# Revit family: LeL Lira 1.0
name_source: partatom
category: Lighting Fixtures
units: mm (PartAtom-declared; Revit-internal decimal feet)

## family parameters
Cut with Voids When Loaded = Yes
Host = Face
Light Source = No
Part Type = Normal
Room Calculation Point = No
Round Connector Dimension = Use Diameter
Shared = No

## types (4) — shared parameters
Alimentazione = 230 V
Apparent Load = 6 VA
CCT = 3000 K
CRI = 80
Default Elevation = 1219 mm
Description = Outdoor Wall Mounted
IK = IK08
IP = IP65
Lamp = LED
Manufacturer = L&L Luce&Light
Model = LR10
Rated Power supply = 230 V
URL = https://www.lucelight.it
Wattage = 6 W
Weight = 0.53 kg

## per-type parameters (varying)
| type | Finish | Lumen Output | Photometry |
| 1.0 A 6W 230Vac white | LeL White | 368 lm | LR10 Light source : 1.0 A white |
| 1.0 A 6W 230Vac cor-ten | LeL Cor-ten | 278 lm | LR10 Light source : 1.0 A corten |
| 1.0 A 6W 230Vac anthracite | LeL Anthracite | 278 lm | LR10 Light source : 1.0 A antracite |
| 1.0 A 6W 230Vac grey | LeL Grey | 368 lm | LR10 Light source : 1.0 A grey |

## geometry (parser evidence)
native form markers: Sweep x1
no freeform markers — native parametric forms only
